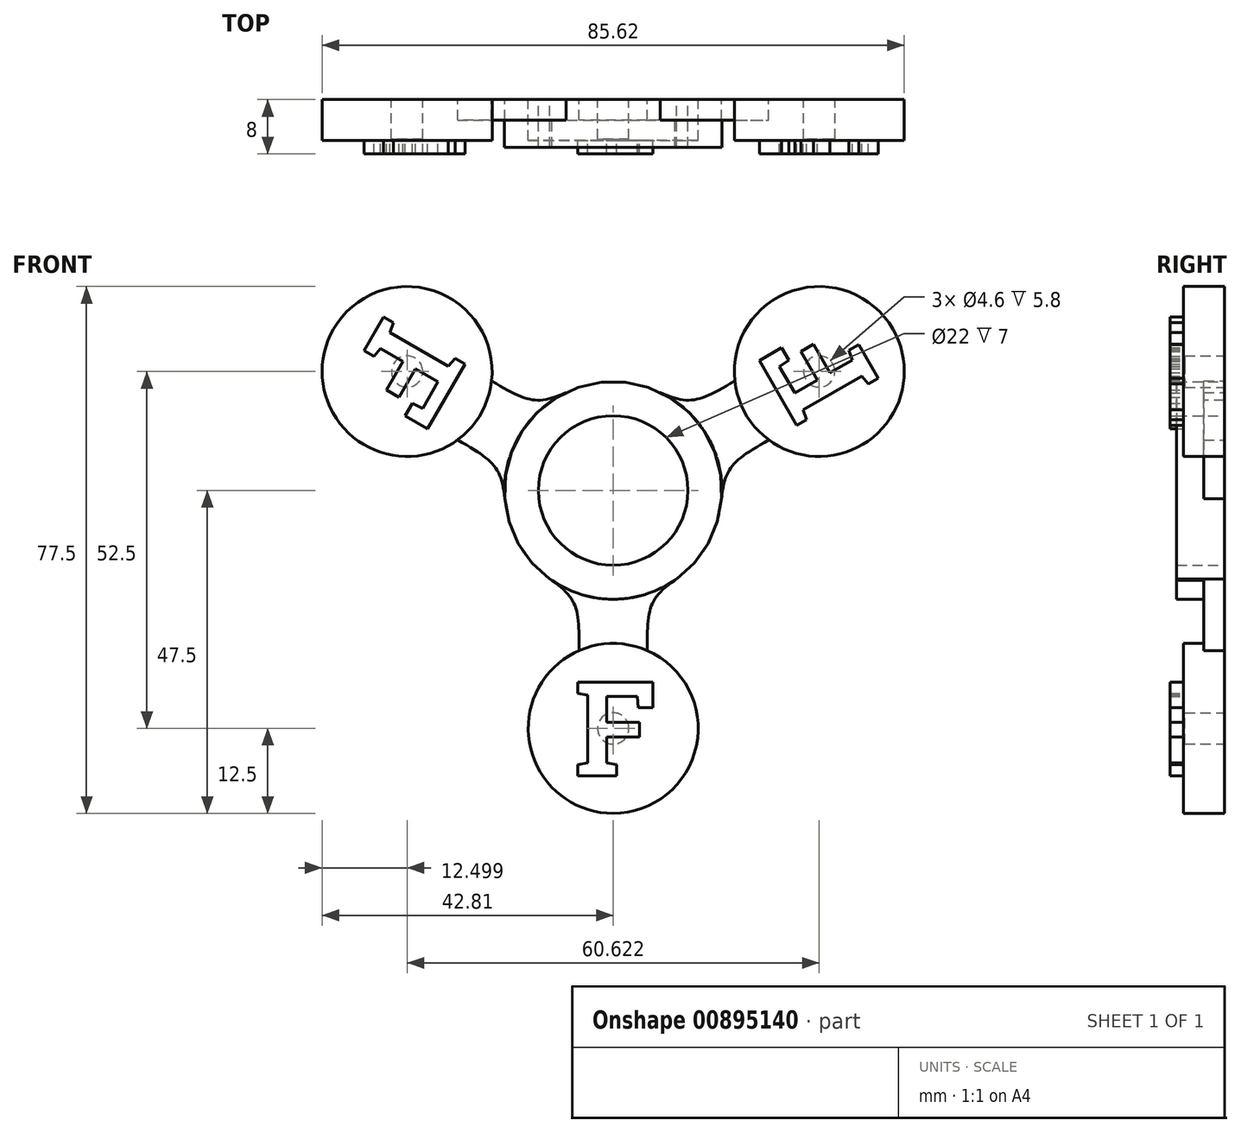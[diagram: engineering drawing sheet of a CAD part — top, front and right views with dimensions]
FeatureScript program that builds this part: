
annotation { "Feature Type Name" : "Feature", "Feature Type Description" : "" }
export const myFeature = defineFeature(function(context is Context, id is Id, definition is map)
    precondition{}
    {
        {
            var Q0;
            Q0=qCreatedBy(makeId("Front.planeOp"),FACE);
            var sketch = newSketch(context, id + "F0", { "sketchPlane" : qUnion([Q0])});
            skCircle(sketch, "E0", {"center": v(0, 0) * mm, "radius": 11 * mm});
            skCircle(sketch, "E1", {"center": v(0, 0) * mm, "radius": 16 * mm});
            skLineSegment(sketch, "E2.top", {"start": v(-5, -35) * mm, "end": v(5, -35) * mm});
            skFitSpline(sketch, "E3", {"points": [v(-9.33, -13) * mm, v(-5, -24) * mm], "startDerivative": vector(12.98, -9) * mm, "endDerivative": vector(0, -19.5) * mm});
            skFitSpline(sketch, "E4", {"points": [v(9.33, -13) * mm, v(5, -24) * mm], "startDerivative": vector(-12.98, -9) * mm, "endDerivative": vector(0, -19.5) * mm});
            skLineSegment(sketch, "E5", {"start": v(5, -24) * mm, "end": v(5, -35) * mm});
            skLineSegment(sketch, "E6", {"start": v(-5, -24) * mm, "end": v(-5, -35) * mm});
            skSolve(sketch);
        }
        {
            var Q0;
            Q0=qCreatedBy(makeId("Front.planeOp"),FACE);
            var sketch = newSketch(context, id + "F1", { "sketchPlane" : qUnion([Q0])});
            skText(sketch, "E7", { "text": "F", "fontName": "RobotoSlab-Bold.ttf"});
            const initialGuessF1  = {"E7": [-0.00573, -0.042, 1, 0, 0.014]};
            skSetInitialGuess(sketch, initialGuessF1);
            skSolve(sketch);
        }
        {
            var Q0;
            Q0=makeQuery(id+"F0.imprint","IMPRINT",FACE,{"disambiguationData":[TD([[makeQuery(id+"F0.imprint","IMPRINT",EDGE,{"derivedFrom":sQuery(id+"F0.wireOp",EDGE,"E0")}),-1.0]])]});
            extrude(context, id + "F2", {"entities" : qUnion([Q0]), "depth" : 7 * mm, "offsetDistance" : 25 * mm});
        }
        {
            var Q0;
            Q0 = qSketchRegion(id + "F0", true);
            extrude(context, id + "F3", {"entities" : qUnion([Q0]), "operationType" : NewBodyOperationType.ADD, "depth" : 3 * mm, "offsetDistance" : 25 * mm});
        }
        {
            var Q0;
            Q0 = qSketchRegion(id + "F1", true);
            extrude(context, id + "F4", {"entities" : qUnion([Q0]), "operationType" : NewBodyOperationType.ADD, "depth" : 8 * mm, "offsetDistance" : 25 * mm});
        }
        {
            var Q0;
            Q0=qCreatedBy(makeId("Front.planeOp"),FACE);
            var sketch = newSketch(context, id + "F5", { "sketchPlane" : qUnion([Q0])});
            skCircle(sketch, "E8", {"center": v(0, -35) * mm, "radius": 12.5 * mm});
            skSolve(sketch);
        }
        {
            var Q0;
            Q0=qCreatedBy(makeId("Front.planeOp"),FACE);
            var sketch = newSketch(context, id + "F6", { "sketchPlane" : qUnion([Q0])});
            skCircle(sketch, "E9", {"center": v(0, -35) * mm, "radius": 2.3 * mm});
            skSolve(sketch);
        }
        {
            var Q0;
            Q0=makeQuery(id+"F5.imprint","IMPRINT",FACE,{"disambiguationData":[TD([[makeQuery(id+"F5.imprint","IMPRINT",EDGE,{"derivedFrom":sQuery(id+"F5.wireOp",EDGE,"E8")}),1.0]])]});
            extrude(context, id + "F7", {"entities" : qUnion([Q0]), "operationType" : NewBodyOperationType.ADD, "depth" : 6 * mm, "offsetDistance" : 25 * mm});
        }
        {
            var Q0;
            Q0=makeQuery(id+"F6.imprint","IMPRINT",FACE,{"disambiguationData":[TD([[makeQuery(id+"F6.imprint","IMPRINT",EDGE,{"derivedFrom":sQuery(id+"F6.wireOp",EDGE,"E9")}),1.0]])]});
            extrude(context, id + "F8", {"entities" : qUnion([Q0]), "operationType" : NewBodyOperationType.REMOVE, "oppositeDirection" : true, "depth" : -5.8 * mm, "offsetDistance" : 25 * mm});
        }
        {
            var Q0;
            Q0=makeQuery(id+"F2.opExtrude","SWEPT_BODY",BODY,{"disambiguationData":[OSD([sQuery(id+"F0.wireOp",EDGE,"E0"),sQuery(id+"F0.wireOp",EDGE,"E1"),sQuery(id+"F0.wireOp",EDGE,"E3"),sQuery(id+"F0.wireOp",EDGE,"E4")])]});
            var Q1;
            Q1=makeQuery(id+"F2.opExtrude","CAP_EDGE",EDGE,{"disambiguationData":[OSD([sQuery(id+"F0.wireOp",EDGE,"E0")])],"isStart":false});
            circularPattern(context, id + "F9", {"operationType" : NewBodyOperationType.ADD, "entities" : qUnion([Q0]), "axis" : qUnion([Q1]), "angle" : 360 * degree, "instanceCount" : 3, "equalSpace" : true});
        }
    });
